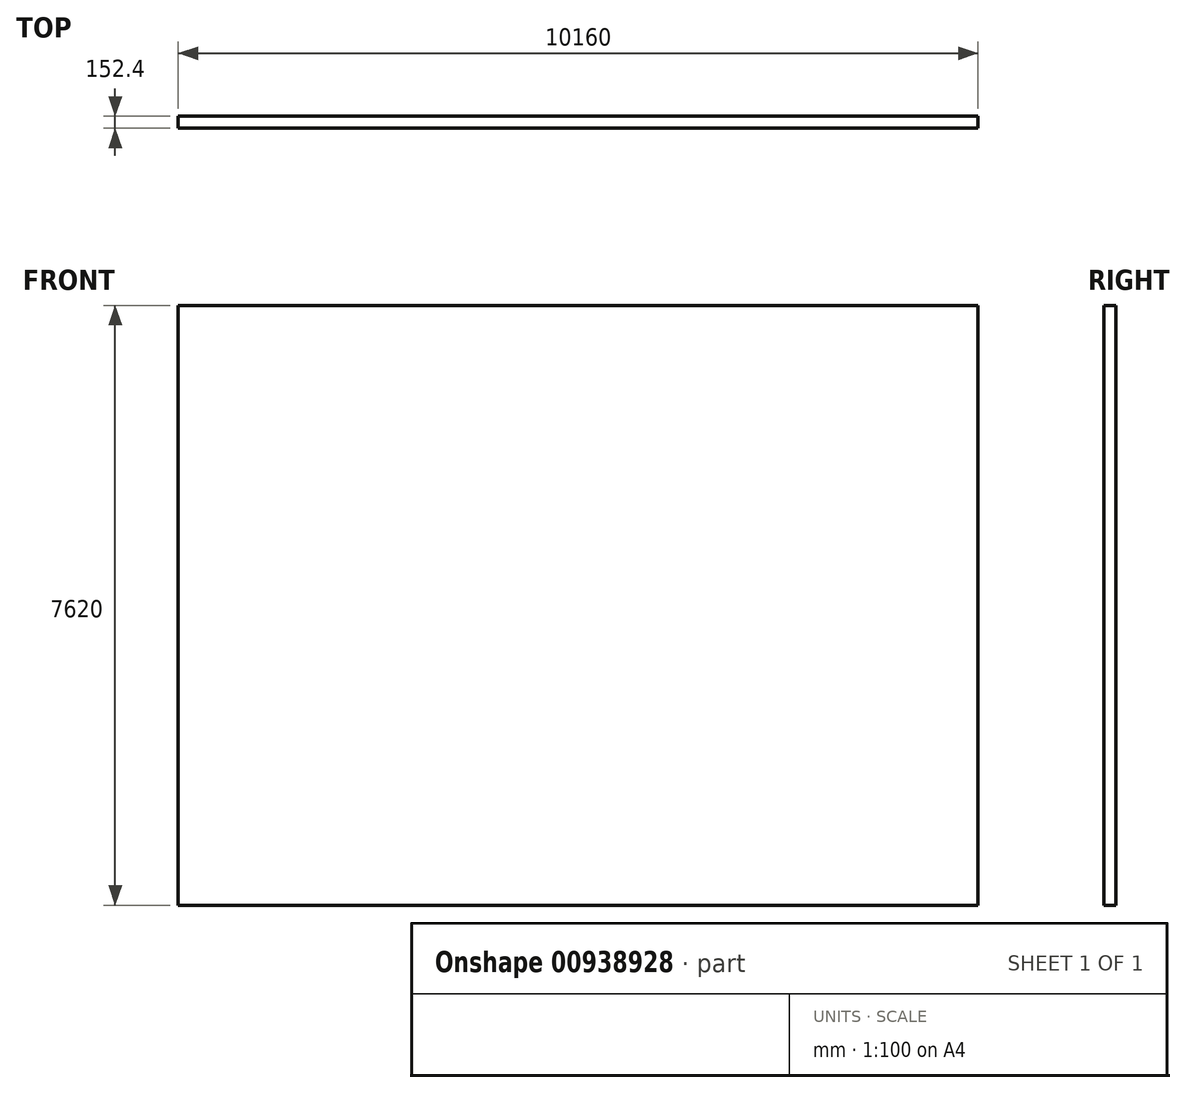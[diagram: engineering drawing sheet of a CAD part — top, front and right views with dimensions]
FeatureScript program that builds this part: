
annotation { "Feature Type Name" : "Feature", "Feature Type Description" : "" }
export const myFeature = defineFeature(function(context is Context, id is Id, definition is map)
    precondition{}
    {
        {
            var Q0;
            Q0=qCreatedBy(makeId("Front.planeOp"),FACE);
            var sketch = newSketch(context, id + "F0", { "sketchPlane" : qUnion([Q0])});
            skLineSegment(sketch, "E0.bottom", {"start": v(-5080, 3810) * mm, "end": v(5080, 3810) * mm});
            skLineSegment(sketch, "E0.top", {"start": v(-5080, -3810) * mm, "end": v(5080, -3810) * mm});
            skLineSegment(sketch, "E0.left", {"start": v(-5080, 3810) * mm, "end": v(-5080, -3810) * mm});
            skLineSegment(sketch, "E0.right", {"start": v(5080, 3810) * mm, "end": v(5080, -3810) * mm});
            skPoint(sketch, "E0.middle", {"position": v(0, 0) * mm});
            skSolve(sketch);
        }
        {
            var Q0;
            Q0=makeQuery(id+"F0.imprint","IMPRINT",FACE,{"disambiguationData":[TD([[makeQuery(id+"F0.imprint","IMPRINT",EDGE,{"derivedFrom":sQuery(id+"F0.wireOp",EDGE,"E0.bottom")}),-1.0]])]});
            extrude(context, id + "F1", {"entities" : qUnion([Q0]), "depth" : 152.4 * mm, "offsetDistance" : 25.4 * mm});
        }
    });
